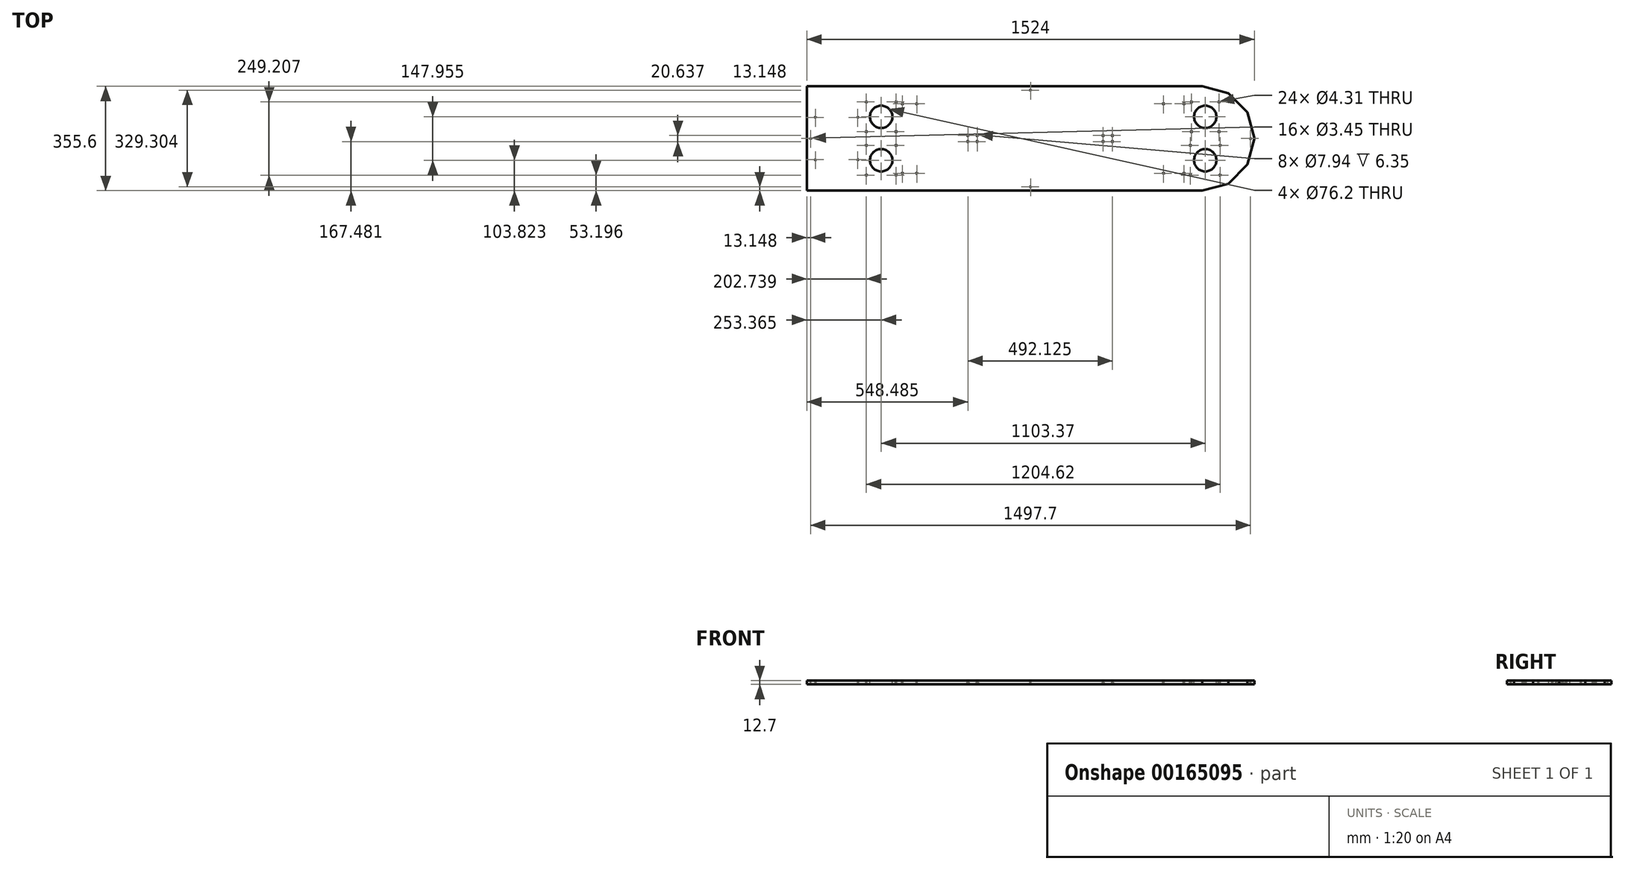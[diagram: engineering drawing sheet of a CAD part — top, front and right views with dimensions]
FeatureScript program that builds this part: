
annotation { "Feature Type Name" : "Feature", "Feature Type Description" : "" }
export const myFeature = defineFeature(function(context is Context, id is Id, definition is map)
    precondition{}
    {
        {
            var Q0;
            Q0=qCreatedBy(makeId("Top.planeOp"),FACE);
            var sketch = newSketch(context, id + "F0", { "sketchPlane" : qUnion([Q0])});
            skLineSegment(sketch, "E0", {"start": v(0, 0) * mm, "end": v(0, -177.8) * mm, "construction": true});
            skLineSegment(sketch, "E1", {"start": v(0, 0) * mm, "end": v(88.9, -153.98) * mm, "construction": true});
            skLineSegment(sketch, "E2", {"start": v(0, 0) * mm, "end": v(153.98, -88.9) * mm, "construction": true});
            skLineSegment(sketch, "E3", {"start": v(0, 0) * mm, "end": v(177.8, 0) * mm, "construction": true});
            skLineSegment(sketch, "E4", {"start": v(0, 0) * mm, "end": v(0, 177.8) * mm, "construction": true});
            skLineSegment(sketch, "E5", {"start": v(0, 0) * mm, "end": v(88.9, 153.98) * mm, "construction": true});
            skLineSegment(sketch, "E6", {"start": v(0, 0) * mm, "end": v(153.98, 88.9) * mm, "construction": true});
            skLineSegment(sketch, "E7", {"start": v(0, 177.8) * mm, "end": v(88.9, 153.98) * mm});
            skLineSegment(sketch, "E8", {"start": v(88.9, 153.98) * mm, "end": v(153.98, 88.9) * mm});
            skLineSegment(sketch, "E9", {"start": v(153.98, 88.9) * mm, "end": v(177.8, 0) * mm});
            skLineSegment(sketch, "E10", {"start": v(177.8, 0) * mm, "end": v(153.98, -88.9) * mm});
            skLineSegment(sketch, "E11", {"start": v(153.98, -88.9) * mm, "end": v(88.9, -153.98) * mm});
            skLineSegment(sketch, "E12", {"start": v(88.9, -153.98) * mm, "end": v(0, -177.8) * mm});
            skLineSegment(sketch, "E13", {"start": v(0, 177.8) * mm, "end": v(-1346.2, 177.8) * mm});
            skLineSegment(sketch, "E14", {"start": v(-1346.2, 177.8) * mm, "end": v(-1346.2, -177.8) * mm});
            skLineSegment(sketch, "E15", {"start": v(-1346.2, -177.8) * mm, "end": v(0, -177.8) * mm});
            skLineSegment(sketch, "E16", {"start": v(-304.8, 0) * mm, "end": v(-304.8, 304.8) * mm, "construction": true});
            skLineSegment(sketch, "E17.bottom", {"start": v(-457.2, 254) * mm, "end": v(-152.4, 254) * mm, "construction": true});
            skLineSegment(sketch, "E17.top", {"start": v(-457.2, 355.6) * mm, "end": v(-152.4, 355.6) * mm, "construction": true});
            skLineSegment(sketch, "E17.left", {"start": v(-457.2, 254) * mm, "end": v(-457.2, 355.6) * mm, "construction": true});
            skLineSegment(sketch, "E17.right", {"start": v(-152.4, 254) * mm, "end": v(-152.4, 355.6) * mm, "construction": true});
            skPoint(sketch, "E17.middle", {"position": v(-304.8, 304.8) * mm});
            skLineSegment(sketch, "E18", {"start": v(0, 0) * mm, "end": v(-304.8, 0) * mm, "construction": true});
            skLineSegment(sketch, "E19", {"start": v(-1346.2, 0) * mm, "end": v(-1244.6, 0) * mm, "construction": true});
            skLineSegment(sketch, "E20.bottom", {"start": v(-1316.83, -72.23) * mm, "end": v(-1172.37, -72.23) * mm, "construction": true});
            skLineSegment(sketch, "E20.top", {"start": v(-1316.83, 72.23) * mm, "end": v(-1172.37, 72.23) * mm, "construction": true});
            skLineSegment(sketch, "E20.left", {"start": v(-1316.83, -72.23) * mm, "end": v(-1316.83, 72.23) * mm, "construction": true});
            skLineSegment(sketch, "E20.right", {"start": v(-1172.37, -72.23) * mm, "end": v(-1172.37, 72.23) * mm, "construction": true});
            skPoint(sketch, "E20.middle", {"position": v(-1244.6, 0) * mm});
            skCircle(sketch, "E21", {"center": v(-1172.37, 72.23) * mm, "radius": 1.73 * mm});
            skCircle(sketch, "E22", {"center": v(-1316.83, 72.23) * mm, "radius": 1.73 * mm});
            skCircle(sketch, "E23", {"center": v(-1316.83, -72.23) * mm, "radius": 1.73 * mm});
            skCircle(sketch, "E24", {"center": v(-1172.37, -72.23) * mm, "radius": 1.73 * mm});
            skSolve(sketch);
        }
        {
            var Q0;
            Q0=makeQuery(id+"F0.imprint","IMPRINT",FACE,{"disambiguationData":[TD([[makeQuery(id+"F0.imprint","IMPRINT",EDGE,{"derivedFrom":sQuery(id+"F0.wireOp",EDGE,"E7")}),-1.0]])]});
            extrude(context, id + "F1", {"entities" : qUnion([Q0]), "depth" : 12.7 * mm});
        }
        {
            var Q0;
            Q0=makeQuery(id+"F1.opExtrude","CAP_FACE",FACE,{"disambiguationData":[OSD([sQuery(id+"F0.wireOp",EDGE,"E7"),sQuery(id+"F0.wireOp",EDGE,"E8"),sQuery(id+"F0.wireOp",EDGE,"E9"),sQuery(id+"F0.wireOp",EDGE,"E10"),sQuery(id+"F0.wireOp",EDGE,"E11"),sQuery(id+"F0.wireOp",EDGE,"E12"),sQuery(id+"F0.wireOp",EDGE,"E13"),sQuery(id+"F0.wireOp",EDGE,"E14"),sQuery(id+"F0.wireOp",EDGE,"E15")])],"isStart":false});
            var sketch = newSketch(context, id + "F2", { "sketchPlane" : qUnion([Q0])});
            skLineSegment(sketch, "E25", {"start": v(164.65, 0) * mm, "end": v(-584.2, 0) * mm, "construction": true});
            skLineSegment(sketch, "E26", {"start": v(-584.2, 0) * mm, "end": v(-1333.05, 0) * mm, "construction": true});
            skLineSegment(sketch, "E27", {"start": v(-1333.05, 0) * mm, "end": v(-1346.2, 0) * mm, "construction": true});
            skLineSegment(sketch, "E28", {"start": v(-584.2, 177.8) * mm, "end": v(-584.2, 164.65) * mm, "construction": true});
            skLineSegment(sketch, "E29", {"start": v(-584.2, 164.65) * mm, "end": v(-584.2, -164.65) * mm, "construction": true});
            skLineSegment(sketch, "E30", {"start": v(-584.2, -164.65) * mm, "end": v(-584.2, -177.8) * mm, "construction": true});
            skCircle(sketch, "E31", {"center": v(-1333.05, 0) * mm, "radius": 1.73 * mm});
            skCircle(sketch, "E32", {"center": v(-584.2, 164.65) * mm, "radius": 1.73 * mm});
            skCircle(sketch, "E33", {"center": v(-584.2, -164.65) * mm, "radius": 1.73 * mm});
            skCircle(sketch, "E34", {"center": v(164.65, 0) * mm, "radius": 1.73 * mm});
            skPoint(sketch, "E35.middle", {"position": v(-584.2, 0) * mm});
            skCircle(sketch, "E36", {"center": v(10.53, 73.98) * mm, "radius": 38.1 * mm});
            skCircle(sketch, "E37", {"center": v(10.53, -73.98) * mm, "radius": 38.1 * mm});
            skCircle(sketch, "E38", {"center": v(-1092.84, 73.98) * mm, "radius": 38.1 * mm});
            skCircle(sketch, "E39", {"center": v(-1092.83, -73.98) * mm, "radius": 38.1 * mm});
            skLineSegment(sketch, "E40.bottom", {"start": v(-36.44, 124.6) * mm, "end": v(57.5, 124.6) * mm, "construction": true});
            skLineSegment(sketch, "E40.top", {"start": v(-36.44, 23.35) * mm, "end": v(57.5, 23.35) * mm, "construction": true});
            skLineSegment(sketch, "E40.left", {"start": v(-36.44, 124.6) * mm, "end": v(-36.44, 23.35) * mm, "construction": true});
            skLineSegment(sketch, "E40.right", {"start": v(57.5, 124.6) * mm, "end": v(57.5, 23.35) * mm, "construction": true});
            skLineSegment(sketch, "E41.bottom", {"start": v(-40.1, -124.6) * mm, "end": v(61.16, -124.6) * mm, "construction": true});
            skLineSegment(sketch, "E41.top", {"start": v(-40.1, -23.35) * mm, "end": v(61.16, -23.35) * mm, "construction": true});
            skLineSegment(sketch, "E41.left", {"start": v(-40.1, -124.6) * mm, "end": v(-40.1, -23.35) * mm, "construction": true});
            skLineSegment(sketch, "E41.right", {"start": v(61.16, -124.6) * mm, "end": v(61.16, -23.35) * mm, "construction": true});
            skLineSegment(sketch, "E42.bottom", {"start": v(-1143.46, 124.6) * mm, "end": v(-1042.2, 124.6) * mm, "construction": true});
            skLineSegment(sketch, "E42.top", {"start": v(-1143.46, 23.35) * mm, "end": v(-1042.2, 23.35) * mm, "construction": true});
            skLineSegment(sketch, "E42.left", {"start": v(-1143.46, 124.6) * mm, "end": v(-1143.46, 23.35) * mm, "construction": true});
            skLineSegment(sketch, "E42.right", {"start": v(-1042.2, 124.6) * mm, "end": v(-1042.2, 23.35) * mm, "construction": true});
            skLineSegment(sketch, "E43.bottom", {"start": v(-1143.46, -124.6) * mm, "end": v(-1042.2, -124.6) * mm, "construction": true});
            skLineSegment(sketch, "E43.top", {"start": v(-1143.46, -23.35) * mm, "end": v(-1042.2, -23.35) * mm, "construction": true});
            skLineSegment(sketch, "E43.left", {"start": v(-1143.46, -124.6) * mm, "end": v(-1143.46, -23.35) * mm, "construction": true});
            skLineSegment(sketch, "E43.right", {"start": v(-1042.2, -124.6) * mm, "end": v(-1042.2, -23.35) * mm, "construction": true});
            skCircle(sketch, "E44", {"center": v(-40.1, -124.6) * mm, "radius": 2.15 * mm});
            skCircle(sketch, "E45", {"center": v(61.16, -124.6) * mm, "radius": 2.15 * mm});
            skCircle(sketch, "E46", {"center": v(61.16, -23.35) * mm, "radius": 2.15 * mm});
            skCircle(sketch, "E47", {"center": v(-40.1, -23.35) * mm, "radius": 2.15 * mm});
            skCircle(sketch, "E48", {"center": v(-36.44, 23.35) * mm, "radius": 2.15 * mm});
            skCircle(sketch, "E49", {"center": v(-36.44, 124.6) * mm, "radius": 2.15 * mm});
            skCircle(sketch, "E50", {"center": v(57.5, 124.6) * mm, "radius": 2.15 * mm});
            skCircle(sketch, "E51", {"center": v(57.5, 124.6) * mm, "radius": 3.97 * mm, "construction": true});
            skCircle(sketch, "E52", {"center": v(-1092.84, 73.98) * mm, "radius": 75.57 * mm, "construction": true});
            skLineSegment(sketch, "E53.bottom", {"start": v(-1316.83, 72.23) * mm, "end": v(-1172.37, 72.23) * mm, "construction": true});
            skLineSegment(sketch, "E53.top", {"start": v(-1316.83, -72.23) * mm, "end": v(-1172.37, -72.23) * mm, "construction": true});
            skLineSegment(sketch, "E53.left", {"start": v(-1316.83, 72.23) * mm, "end": v(-1316.83, -72.23) * mm, "construction": true});
            skLineSegment(sketch, "E53.right", {"start": v(-1172.37, 72.23) * mm, "end": v(-1172.37, -72.23) * mm, "construction": true});
            skPoint(sketch, "E53.middle", {"position": v(-1244.6, 0) * mm});
            skCircle(sketch, "E54", {"center": v(-1172.37, 72.23) * mm, "radius": 3.97 * mm, "construction": true});
            skLineSegment(sketch, "E55", {"start": v(-1168.4, 72.23) * mm, "end": v(-1168.4, 0) * mm, "construction": true});
            skCircle(sketch, "E56", {"center": v(57.5, 23.35) * mm, "radius": 2.15 * mm});
            skCircle(sketch, "E57", {"center": v(-1143.46, -124.6) * mm, "radius": 2.15 * mm});
            skCircle(sketch, "E58", {"center": v(-1042.2, -124.6) * mm, "radius": 2.15 * mm});
            skCircle(sketch, "E59", {"center": v(-1042.2, -23.35) * mm, "radius": 2.15 * mm});
            skCircle(sketch, "E60", {"center": v(-1143.46, -23.35) * mm, "radius": 2.15 * mm});
            skCircle(sketch, "E61", {"center": v(-1143.46, 23.35) * mm, "radius": 2.15 * mm});
            skCircle(sketch, "E62", {"center": v(-1042.2, 23.35) * mm, "radius": 2.15 * mm});
            skCircle(sketch, "E63", {"center": v(-1042.2, 124.6) * mm, "radius": 2.15 * mm});
            skCircle(sketch, "E64", {"center": v(-1143.46, 124.6) * mm, "radius": 2.15 * mm});
            skLineSegment(sketch, "E65.right", {"start": v(-1092.83, 73.98) * mm, "end": v(-1092.83, -73.98) * mm, "construction": true});
            skPoint(sketch, "E66", {"position": v(-1092.83, 0) * mm});
            skLineSegment(sketch, "E67", {"start": v(61.16, -73.98) * mm, "end": v(-40.1, -73.98) * mm, "construction": true});
            skLineSegment(sketch, "E68", {"start": v(57.5, 73.98) * mm, "end": v(-36.44, 73.98) * mm, "construction": true});
            skLineSegment(sketch, "E69", {"start": v(0, 177.8) * mm, "end": v(0, 152.4) * mm, "construction": true});
            skLineSegment(sketch, "E70", {"start": v(0, 152.4) * mm, "end": v(76.2, 131.98) * mm, "construction": true});
            skCircle(sketch, "E71", {"center": v(164.65, 0) * mm, "radius": 12.7 * mm, "construction": true});
            skLineSegment(sketch, "E72", {"start": v(88.9, 153.98) * mm, "end": v(76.2, 131.98) * mm, "construction": true});
            skLineSegment(sketch, "E73", {"start": v(76.2, 131.98) * mm, "end": v(0, 0) * mm, "construction": true});
            skLineSegment(sketch, "E74", {"start": v(0, 152.4) * mm, "end": v(-78.89, 152.4) * mm, "construction": true});
            skCircle(sketch, "E75", {"center": v(10.53, 73.98) * mm, "radius": 73.03 * mm, "construction": true});
            skLineSegment(sketch, "E76", {"start": v(10.53, 73.98) * mm, "end": v(10.53, -73.98) * mm, "construction": true});
            skCircle(sketch, "E77", {"center": v(-1143.46, 124.6) * mm, "radius": 3.97 * mm, "construction": true});
            skPoint(sketch, "E78", {"position": v(10.53, 0) * mm});
            skLineSegment(sketch, "E79", {"start": v(177.8, 0) * mm, "end": v(177.8, -1701.8) * mm, "construction": true});
            skLineSegment(sketch, "E80", {"start": v(177.8, -1701.8) * mm, "end": v(-1346.2, -1701.8) * mm, "construction": true});
            skLineSegment(sketch, "E81", {"start": v(-1346.2, -1701.8) * mm, "end": v(-1346.2, -177.8) * mm, "construction": true});
            skLineSegment(sketch, "E82", {"start": v(-584.2, -177.8) * mm, "end": v(-584.2, -1701.8) * mm, "construction": true});
            skSolve(sketch);
        }
        {
            var Q0;
            Q0 = qSketchRegion(id + "F2", true);
            var Q1;
            Q1=makeQuery(id+"F1.opExtrude","CAP_FACE",FACE,{"disambiguationData":[OSD([sQuery(id+"F0.wireOp",EDGE,"E7"),sQuery(id+"F0.wireOp",EDGE,"E8"),sQuery(id+"F0.wireOp",EDGE,"E9"),sQuery(id+"F0.wireOp",EDGE,"E10"),sQuery(id+"F0.wireOp",EDGE,"E11"),sQuery(id+"F0.wireOp",EDGE,"E12"),sQuery(id+"F0.wireOp",EDGE,"E13"),sQuery(id+"F0.wireOp",EDGE,"E14"),sQuery(id+"F0.wireOp",EDGE,"E15")])],"isStart":true});
            extrude(context, id + "F3", {"entities" : qUnion([Q0]), "operationType" : NewBodyOperationType.REMOVE, "endBound" : BoundingType.UP_TO_SURFACE, "oppositeDirection" : true, "endBoundEntityFace" : qUnion([Q1]), "depth" : 25.4 * mm});
        }
        {
            var Q0;
            Q0=makeQuery(id+"F1.opExtrude","CAP_FACE",FACE,{"disambiguationData":[OSD([sQuery(id+"F0.wireOp",EDGE,"E7"),sQuery(id+"F0.wireOp",EDGE,"E8"),sQuery(id+"F0.wireOp",EDGE,"E9"),sQuery(id+"F0.wireOp",EDGE,"E10"),sQuery(id+"F0.wireOp",EDGE,"E11"),sQuery(id+"F0.wireOp",EDGE,"E12"),sQuery(id+"F0.wireOp",EDGE,"E13"),sQuery(id+"F0.wireOp",EDGE,"E14"),sQuery(id+"F0.wireOp",EDGE,"E15")])],"isStart":false});
            var sketch = newSketch(context, id + "F4", { "sketchPlane" : qUnion([Q0])});
            skPoint(sketch, "E83.middle", {"position": v(-551.65, 0) * mm});
            skLineSegment(sketch, "E84", {"start": v(-321.47, 0) * mm, "end": v(-781.84, 0) * mm, "construction": true});
            skLineSegment(sketch, "E85.bottom", {"start": v(-305.6, 10.32) * mm, "end": v(-337.34, 10.32) * mm, "construction": true});
            skLineSegment(sketch, "E85.top", {"start": v(-305.6, -10.32) * mm, "end": v(-337.34, -10.32) * mm, "construction": true});
            skLineSegment(sketch, "E85.left", {"start": v(-305.6, 10.32) * mm, "end": v(-305.6, -10.32) * mm, "construction": true});
            skLineSegment(sketch, "E85.right", {"start": v(-337.34, 10.32) * mm, "end": v(-337.34, -10.32) * mm, "construction": true});
            skPoint(sketch, "E85.middle", {"position": v(-321.47, 0) * mm});
            skLineSegment(sketch, "E86.bottom", {"start": v(-765.97, -10.32) * mm, "end": v(-797.72, -10.32) * mm, "construction": true});
            skLineSegment(sketch, "E86.top", {"start": v(-765.97, 10.32) * mm, "end": v(-797.72, 10.32) * mm, "construction": true});
            skLineSegment(sketch, "E86.left", {"start": v(-765.97, -10.32) * mm, "end": v(-765.97, 10.32) * mm, "construction": true});
            skLineSegment(sketch, "E86.right", {"start": v(-797.72, -10.32) * mm, "end": v(-797.72, 10.32) * mm, "construction": true});
            skPoint(sketch, "E86.middle", {"position": v(-781.84, 0) * mm});
            skCircle(sketch, "E87", {"center": v(-305.6, -10.32) * mm, "radius": 1.73 * mm});
            skCircle(sketch, "E88", {"center": v(-337.34, -10.32) * mm, "radius": 1.73 * mm});
            skCircle(sketch, "E89", {"center": v(-337.34, 10.32) * mm, "radius": 1.73 * mm});
            skCircle(sketch, "E90", {"center": v(-305.6, 10.32) * mm, "radius": 1.73 * mm});
            skCircle(sketch, "E91", {"center": v(-765.97, 10.32) * mm, "radius": 1.73 * mm});
            skCircle(sketch, "E92", {"center": v(-765.97, -10.32) * mm, "radius": 1.73 * mm});
            skCircle(sketch, "E93", {"center": v(-797.72, -10.32) * mm, "radius": 1.73 * mm});
            skCircle(sketch, "E94", {"center": v(-797.72, 10.32) * mm, "radius": 1.73 * mm});
            skLineSegment(sketch, "E95.bottom", {"start": v(-131.6, -118.37) * mm, "end": v(-61.86, -118.37) * mm, "construction": true});
            skLineSegment(sketch, "E95.top", {"start": v(-131.6, 118.37) * mm, "end": v(-61.86, 118.37) * mm, "construction": true});
            skLineSegment(sketch, "E95.left", {"start": v(-131.6, -118.37) * mm, "end": v(-131.6, 118.37) * mm, "construction": true});
            skLineSegment(sketch, "E95.right", {"start": v(-61.86, -118.37) * mm, "end": v(-61.86, 118.37) * mm, "construction": true});
            skPoint(sketch, "E95.middle", {"position": v(-96.73, 0) * mm});
            skCircle(sketch, "E96", {"center": v(-61.86, 118.37) * mm, "radius": 2.15 * mm});
            skCircle(sketch, "E97", {"center": v(-131.6, 118.37) * mm, "radius": 2.15 * mm});
            skCircle(sketch, "E98", {"center": v(-131.6, -118.37) * mm, "radius": 2.15 * mm});
            skCircle(sketch, "E99", {"center": v(-61.86, -118.37) * mm, "radius": 2.15 * mm});
            skLineSegment(sketch, "E100.bottom", {"start": v(-971.7, -118.37) * mm, "end": v(-1020.44, -118.37) * mm, "construction": true});
            skLineSegment(sketch, "E100.top", {"start": v(-971.7, 118.37) * mm, "end": v(-1020.44, 118.37) * mm, "construction": true});
            skLineSegment(sketch, "E100.left", {"start": v(-971.7, -118.37) * mm, "end": v(-971.7, 118.37) * mm, "construction": true});
            skLineSegment(sketch, "E100.right", {"start": v(-1020.44, -118.37) * mm, "end": v(-1020.44, 118.37) * mm, "construction": true});
            skPoint(sketch, "E100.middle", {"position": v(-996.08, 0) * mm});
            skCircle(sketch, "E101", {"center": v(10.53, -73.98) * mm, "radius": 72.4 * mm, "construction": true});
            skCircle(sketch, "E102", {"center": v(-1092.83, -73.98) * mm, "radius": 72.4 * mm, "construction": true});
            skCircle(sketch, "E103", {"center": v(-1020.44, -118.37) * mm, "radius": 2.15 * mm});
            skCircle(sketch, "E104", {"center": v(-971.7, -118.37) * mm, "radius": 2.15 * mm});
            skCircle(sketch, "E105", {"center": v(-1020.44, 118.37) * mm, "radius": 2.15 * mm});
            skCircle(sketch, "E106", {"center": v(-971.7, 118.37) * mm, "radius": 2.15 * mm});
            skLineSegment(sketch, "E107", {"start": v(-971.7, 0) * mm, "end": v(-781.84, 0) * mm, "construction": true});
            skLineSegment(sketch, "E108", {"start": v(-131.6, 0) * mm, "end": v(-321.47, 0) * mm, "construction": true});
            skSolve(sketch);
        }
        {
            var Q0;
            Q0 = qSketchRegion(id + "F4", true);
            var Q1;
            Q1=makeQuery(id+"F1.opExtrude","CAP_FACE",FACE,{"disambiguationData":[OSD([sQuery(id+"F0.wireOp",EDGE,"E7"),sQuery(id+"F0.wireOp",EDGE,"E8"),sQuery(id+"F0.wireOp",EDGE,"E9"),sQuery(id+"F0.wireOp",EDGE,"E10"),sQuery(id+"F0.wireOp",EDGE,"E11"),sQuery(id+"F0.wireOp",EDGE,"E12"),sQuery(id+"F0.wireOp",EDGE,"E13"),sQuery(id+"F0.wireOp",EDGE,"E14"),sQuery(id+"F0.wireOp",EDGE,"E15")])],"isStart":true});
            extrude(context, id + "F5", {"entities" : qUnion([Q0]), "operationType" : NewBodyOperationType.REMOVE, "endBound" : BoundingType.UP_TO_SURFACE, "oppositeDirection" : true, "endBoundEntityFace" : qUnion([Q1]), "depth" : 25.4 * mm});
        }
        {
            var Q0;
            Q0=makeQuery(id+"F1.opExtrude","CAP_FACE",FACE,{"disambiguationData":[OSD([sQuery(id+"F0.wireOp",EDGE,"E7"),sQuery(id+"F0.wireOp",EDGE,"E8"),sQuery(id+"F0.wireOp",EDGE,"E9"),sQuery(id+"F0.wireOp",EDGE,"E10"),sQuery(id+"F0.wireOp",EDGE,"E11"),sQuery(id+"F0.wireOp",EDGE,"E12"),sQuery(id+"F0.wireOp",EDGE,"E13"),sQuery(id+"F0.wireOp",EDGE,"E14"),sQuery(id+"F0.wireOp",EDGE,"E15"),sQuery(id+"F0.wireOp",EDGE,"E21"),sQuery(id+"F0.wireOp",EDGE,"E22"),sQuery(id+"F0.wireOp",EDGE,"E23"),sQuery(id+"F0.wireOp",EDGE,"E24")])],"isStart":true});
            var sketch = newSketch(context, id + "F6", { "sketchPlane" : qUnion([Q0])});
            skCircle(sketch, "E109", {"center": v(-797.72, -10.32) * mm, "radius": 3.97 * mm});
            skCircle(sketch, "E110", {"center": v(-765.97, -10.32) * mm, "radius": 3.97 * mm});
            skCircle(sketch, "E111", {"center": v(-765.97, 10.32) * mm, "radius": 3.97 * mm});
            skCircle(sketch, "E112", {"center": v(-797.72, 10.32) * mm, "radius": 3.97 * mm});
            skCircle(sketch, "E113", {"center": v(-305.6, -10.32) * mm, "radius": 3.97 * mm});
            skCircle(sketch, "E114", {"center": v(-305.6, 10.32) * mm, "radius": 3.97 * mm});
            skCircle(sketch, "E115", {"center": v(-337.34, 10.32) * mm, "radius": 3.97 * mm});
            skCircle(sketch, "E116", {"center": v(-337.34, -10.32) * mm, "radius": 3.97 * mm});
            skSolve(sketch);
        }
        {
            var Q0;
            Q0 = qSketchRegion(id + "F6", true);
            extrude(context, id + "F7", {"entities" : qUnion([Q0]), "operationType" : NewBodyOperationType.REMOVE, "oppositeDirection" : true, "depth" : 6.35 * mm});
        }
    });
